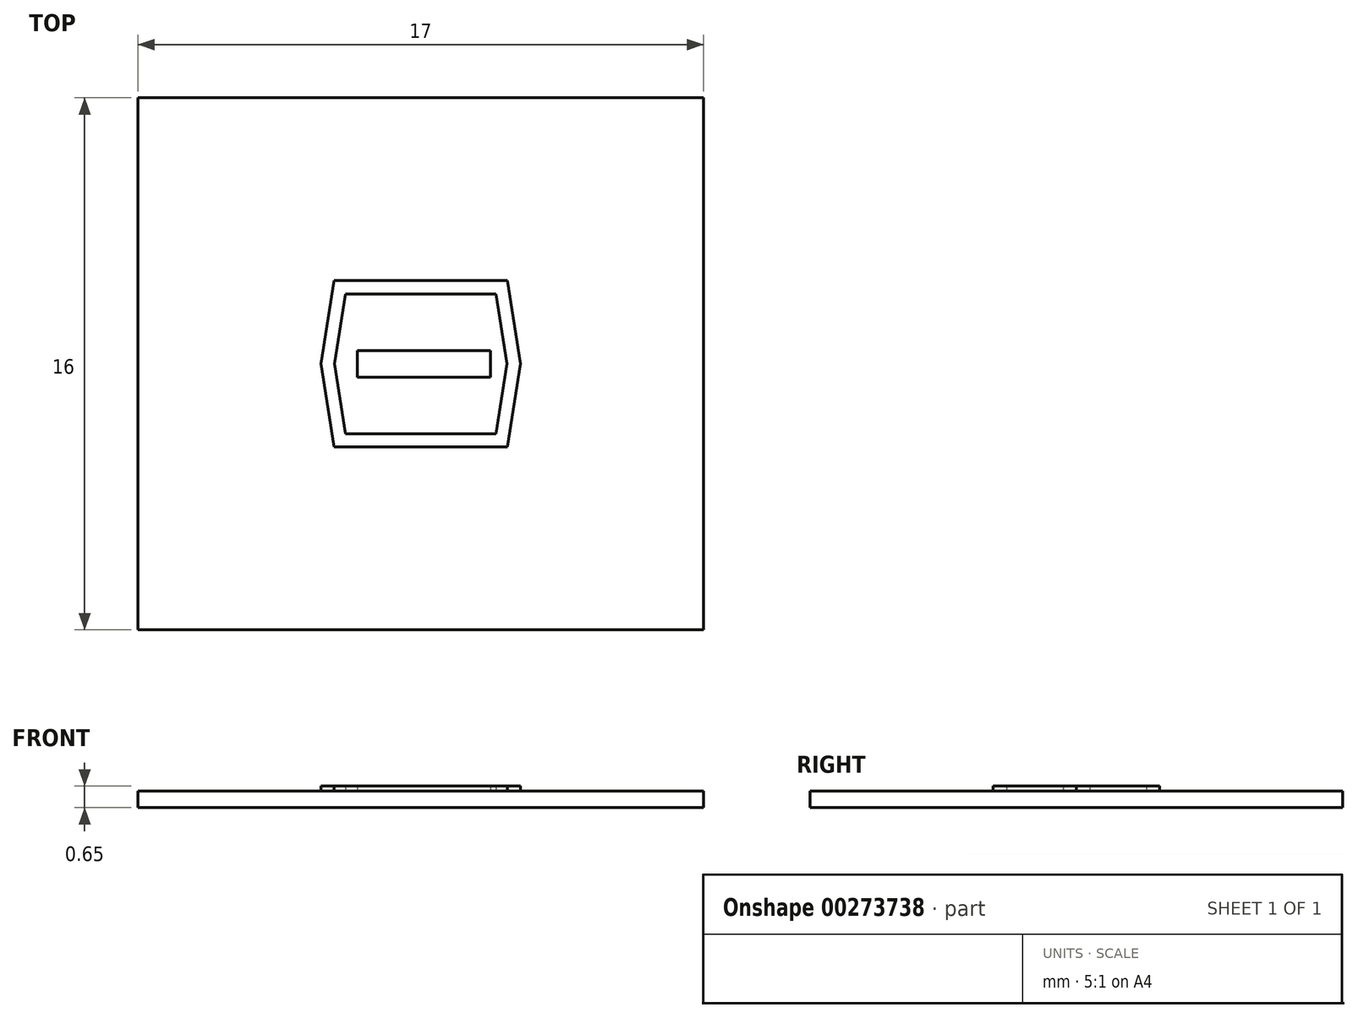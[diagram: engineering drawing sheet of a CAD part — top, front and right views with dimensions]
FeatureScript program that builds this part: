
annotation { "Feature Type Name" : "Feature", "Feature Type Description" : "" }
export const myFeature = defineFeature(function(context is Context, id is Id, definition is map)
    precondition{}
    {
        {
            var Q0;
            Q0=qCreatedBy(makeId("Top.planeOp"),FACE);
            var sketch = newSketch(context, id + "F0", { "sketchPlane" : qUnion([Q0])});
            skLineSegment(sketch, "E0.bottom", {"start": v(0, 0) * mm, "end": v(7, 0) * mm});
            skLineSegment(sketch, "E0.top", {"start": v(0, -6) * mm, "end": v(7, -6) * mm});
            skLineSegment(sketch, "E0.left", {"start": v(0, 0) * mm, "end": v(0, -6) * mm});
            skLineSegment(sketch, "E0.right", {"start": v(7, 0) * mm, "end": v(7, -6) * mm});
            skLineSegment(sketch, "E1", {"start": v(0.5, -3) * mm, "end": v(0.9, -0.5) * mm});
            skPoint(sketch, "E1.startSnap0", {"position": v(0, -3) * mm});
            skLineSegment(sketch, "E2", {"start": v(0.9, -0.5) * mm, "end": v(6.1, -0.5) * mm});
            skLineSegment(sketch, "E3", {"start": v(6.1, -0.5) * mm, "end": v(6.5, -3) * mm});
            skPoint(sketch, "E3.endSnap0", {"position": v(7, -3) * mm});
            skLineSegment(sketch, "E4", {"start": v(6.5, -3) * mm, "end": v(6.1, -5.5) * mm});
            skLineSegment(sketch, "E5", {"start": v(6.1, -5.5) * mm, "end": v(0.9, -5.5) * mm});
            skLineSegment(sketch, "E6", {"start": v(0.9, -5.5) * mm, "end": v(0.5, -3) * mm});
            skLineSegment(sketch, "E7.0", {"start": v(0.9, -3) * mm, "end": v(1.24, -0.9) * mm});
            skLineSegment(sketch, "E7.1", {"start": v(5.76, -0.9) * mm, "end": v(6.1, -3) * mm});
            skLineSegment(sketch, "E7.2", {"start": v(6.1, -3) * mm, "end": v(5.76, -5.1) * mm});
            skLineSegment(sketch, "E7.3", {"start": v(1.24, -0.9) * mm, "end": v(5.76, -0.9) * mm});
            skLineSegment(sketch, "E7.4", {"start": v(5.76, -5.1) * mm, "end": v(1.24, -5.1) * mm});
            skLineSegment(sketch, "E7.5", {"start": v(1.24, -5.1) * mm, "end": v(0.9, -3) * mm});
            skLineSegment(sketch, "E8.bottom", {"start": v(1.6, -2.6) * mm, "end": v(5.6, -2.6) * mm});
            skLineSegment(sketch, "E8.top", {"start": v(1.6, -3.4) * mm, "end": v(5.6, -3.4) * mm});
            skLineSegment(sketch, "E8.left", {"start": v(1.6, -2.6) * mm, "end": v(1.6, -3.4) * mm});
            skLineSegment(sketch, "E8.right", {"start": v(5.6, -2.6) * mm, "end": v(5.6, -3.4) * mm});
            skPoint(sketch, "E9", {"position": v(1.6, -3) * mm});
            skLineSegment(sketch, "E10", {"start": v(0, -3) * mm, "end": v(7, -3) * mm, "construction": true});
            skSolve(sketch);
        }
        {
            var Q0;
            Q0=qCreatedBy(makeId("Top.planeOp"),FACE);
            var sketch = newSketch(context, id + "F1", { "sketchPlane" : qUnion([Q0])});
            skLineSegment(sketch, "E11.0", {"start": v(-5, 5) * mm, "end": v(12, 5) * mm});
            skLineSegment(sketch, "E11.1", {"start": v(-5, 5) * mm, "end": v(-5, -11) * mm});
            skLineSegment(sketch, "E11.2", {"start": v(-5, -11) * mm, "end": v(12, -11) * mm});
            skLineSegment(sketch, "E11.3", {"start": v(12, 5) * mm, "end": v(12, -11) * mm});
            skSolve(sketch);
        }
        {
            var Q0;
            Q0=makeQuery(id+"F0.imprint","IMPRINT",FACE,{"disambiguationData":[TD([[makeQuery(id+"F0.imprint","IMPRINT",EDGE,{"derivedFrom":sQuery(id+"F0.wireOp",EDGE,"E1")}),-1.0]])]});
            var Q1;
            Q1=makeQuery(id+"F0.imprint","IMPRINT",FACE,{"disambiguationData":[TD([[makeQuery(id+"F0.imprint","IMPRINT",EDGE,{"derivedFrom":sQuery(id+"F0.wireOp",EDGE,"E8.bottom")}),-1.0]])]});
            extrude(context, id + "F2", {"entities" : qUnion([Q0, Q1]), "depth" : 0.15 * mm});
        }
        {
            var Q0;
            Q0=makeQuery(id+"F0.imprint","IMPRINT",FACE,{"disambiguationData":[TD([[makeQuery(id+"F0.imprint","IMPRINT",EDGE,{"derivedFrom":sQuery(id+"F0.wireOp",EDGE,"E0.bottom")}),-1.0]])]});
            var Q1;
            Q1=makeQuery(id+"F0.imprint","IMPRINT",FACE,{"disambiguationData":[TD([[makeQuery(id+"F0.imprint","IMPRINT",EDGE,{"derivedFrom":sQuery(id+"F0.wireOp",EDGE,"E7.0")}),-1.0]])]});
            var Q2;
            Q2=makeQuery(id+"F0.imprint","IMPRINT",FACE,{"disambiguationData":[TD([[makeQuery(id+"F0.imprint","IMPRINT",EDGE,{"derivedFrom":sQuery(id+"F0.wireOp",EDGE,"E8.bottom")}),-1.0]])]});
            var Q3;
            Q3=makeQuery(id+"F0.imprint","IMPRINT",FACE,{"disambiguationData":[TD([[makeQuery(id+"F0.imprint","IMPRINT",EDGE,{"derivedFrom":sQuery(id+"F0.wireOp",EDGE,"E1")}),-1.0]])]});
            var Q4;
            Q4=makeQuery(id+"F2.opExtrude","CAP_FACE",FACE,{"disambiguationData":[OSD([sQuery(id+"F1.wireOp",EDGE,"E11.0"),sQuery(id+"F1.wireOp",EDGE,"E11.1"),sQuery(id+"F1.wireOp",EDGE,"E11.2"),sQuery(id+"F1.wireOp",EDGE,"E11.3")])],"isStart":true});
            var Q5;
            Q5=makeQuery(id+"F1.imprint","IMPRINT",FACE,{"disambiguationData":[TD([[makeQuery(id+"F1.imprint","IMPRINT",EDGE,{"derivedFrom":sQuery(id+"F1.wireOp",EDGE,"E11.0")}),-1.0]])]});
            extrude(context, id + "F3", {"entities" : qUnion([Q0, Q1, Q2, Q3, Q4, Q5]), "operationType" : NewBodyOperationType.ADD, "oppositeDirection" : true, "depth" : 0.5 * mm});
        }
    });
